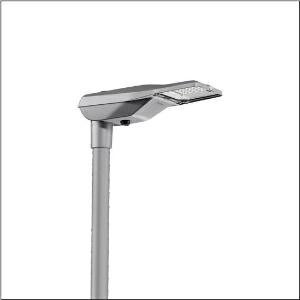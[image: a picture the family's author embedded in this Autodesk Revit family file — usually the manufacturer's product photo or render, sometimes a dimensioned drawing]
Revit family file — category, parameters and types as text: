
# Revit family: streetlight_sl_21_iq_micro___st1_0ab_5xe1m31u08cb_f63b
name_source: partatom
category: Lighting Fixtures
units: mm (PartAtom-declared; Revit-internal decimal feet)

## family parameters
Cut with Voids When Loaded = No
Host = Face
Light Source = No
Part Type = Normal
Room Calculation Point = No
Round Connector Dimension = Use Diameter
Shared = No

## types (1)
- --- (1 x LED, 2530 lm, 19.1 W, 3000K)
    Apparent Load = 19 VA
    CIE Flux Codes = 38 73 97 100 100
    Color Rendering = 70
    Color Temperature = 3000K
    Default Elevation = 1800 mm
    Description = Streetlight SL 21 iQ micro, mast luminaire, primary light control with lens, of PMMA, primary optical cover: cover, of toughened safety glass, transparent, light distribution: ST1.0aB, light emission: direct distribution, primary light characteristic: asymmetric, installation type: post-top, side-entry, LED, High Power LED, rated luminous flux: 2.530lm, luminous efficacy: 133lm/W, light colour: 730, colour temperature: 3000K, control: presetting dimming logarithmic, Street-Remote, Auto-Match, Temp-Guard, Lumen-Switch, Night-Set, Smart-Wire, Light-Fading, Desk-Remote (wireless, voltage-free reading and setting of iQ features in the workshop via application-optimized NFC function/RFID function), optimised constant luminous flux control (CLO 2.0), mains connection: 220..240V, AC, 50/60Hz, start of lifetime: 19W, end of service life: 20W, reduction: 9W, luminaire housing, of diecast aluminium, powder-coated, Siteco® metallic grey (DB 702S), corrosivity category C5 mid according to DIN EN ISO 12944, please order mast flange separately, inclination adjustable: 0°, 5°, 10°, 15°, sealing non-destructively replaceable, multi-level sealing system, length: 528mm, width: 235mm, height: 110mm, mast flange for spigot size: 42mm (side-entry): 5XC10008XM4, 60/48mm (side-entry/post-top): 5XC10108XM2, 76/60mm (side-entry/post-top): 5XC10108XM1, Smart Interface below, protection rating (complete): IP66, insulation class (complete): insulation class II (safety insulation), certification: CE, ENEC, ENEC+, VDE, impact resistance: IK09, permissible operating ambient temperature for outdoor applications: -40..+50°C, standard-compliant lighting for roads and squares, packaging unit: 1 piece

Light Distribution: ST1.0aB
    Height = 110 mm
    Lamp = 1 x LED
    Lamp Light Flux = 2530 lm
    Lamp Power = 19.1 W
    Lamp count = 1
    Length = 528 mm
    Luminous efficacy = 132 lm/W
    Manufacturer = Siteco
    ModVariant = No
    Model = 5XE1M31U08CB
    Number of Poles = 1
    OnlyDefault = Yes
    Power Factor = 1
    Product Name = Streetlight SL 21 iQ micro | ST1.0aB
    Product group = mast luminaire | pylon top
    ProductGroupID = 6100
    Protection Class = Protection class II
    Protection Degree = IP 66
    RLX_Detail_Level = 1
    RLX_Emergency_Light_Flux = 0 lm
    RLX_Emergency_Type = 0
    RLX_Emergency_Type_DB = No
    RlxData = <blob elided: 99169 chars, md5=1be53050>
    Socket = socket
    Standby Power = 0 W
    System Light Flux = 2530 lm
    System Power = 19 W
    Type Comments = factory setting: luminous flux: 100 % | dim-lin: 254 | 387 mA
    Type Image = l_1277290.jpg
    URL = http://relux.com
    VarID = @adj_042907
    Voltage = 0 V
    Weight = 0.00 kg
    Width = 235 mm

## geometry (parser evidence)
native form markers: Blend x4, Sweep x10
no freeform markers — native parametric forms only
